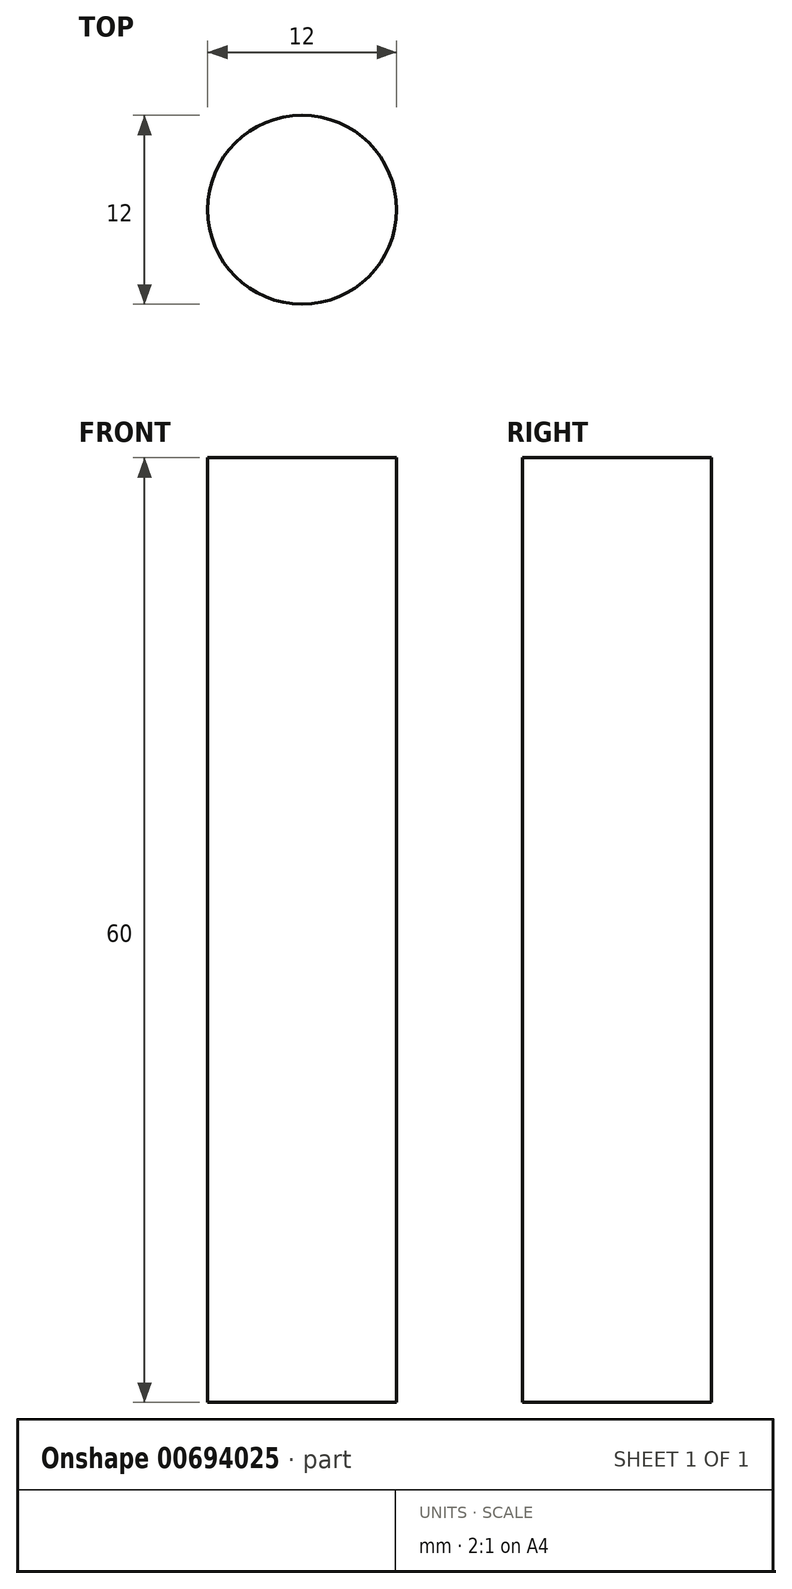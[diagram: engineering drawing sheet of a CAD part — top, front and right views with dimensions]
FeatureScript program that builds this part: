
annotation { "Feature Type Name" : "Feature", "Feature Type Description" : "" }
export const myFeature = defineFeature(function(context is Context, id is Id, definition is map)
    precondition{}
    {
        {
            var Q0;
            Q0=qCreatedBy(makeId("Front.planeOp"),FACE);
            var sketch = newSketch(context, id + "F0", { "sketchPlane" : qUnion([Q0])});
            skLineSegment(sketch, "E0.bottom", {"start": v(0, 0) * mm, "end": v(6, 0) * mm});
            skLineSegment(sketch, "E0.top", {"start": v(0, 60) * mm, "end": v(6, 60) * mm});
            skLineSegment(sketch, "E0.left", {"start": v(0, 0) * mm, "end": v(0, 60) * mm});
            skLineSegment(sketch, "E0.right", {"start": v(6, 0) * mm, "end": v(6, 60) * mm});
            skSolve(sketch);
        }
        {
            var Q0;
            Q0=makeQuery(id+"F0.imprint","IMPRINT",FACE,{"disambiguationData":[TD([[makeQuery(id+"F0.imprint","IMPRINT",EDGE,{"derivedFrom":sQuery(id+"F0.wireOp",EDGE,"E0.bottom")}),1.0]])]});
            var Q1;
            Q1=sQuery(id+"F0.wireOp",EDGE,"E0.left");
            revolve(context, id + "F1", {"entities" : qUnion([Q0]), "axis" : qUnion([Q1]), "revolveType" : RevolveType.FULL});
        }
    });
